# Revit family: Square Diffuser-Round Neck-Return
name_source: partatom
category: Air Terminals
revit_build: Autodesk Revit MEP 2013 (Build: 20120221_2030(x64)
units: mm (PartAtom-declared; Revit-internal decimal feet)

## types (5) — shared parameters

## per-type parameters (varying)
| type | Diffuser Neck Length | Diffuser Neck Width | Diffuser Total Length | Diffuser Total Width | Max Flow |
| 600x600-Square Diffuser-Round Neck-Return | 450 mm | 450 mm | 600 mm  [stored 1.9685 ft] | 600 mm  [stored 1.9685 ft] | 70.0 L/s |
| 525x525-Square Diffuser-Round Neck-Return | 375 mm | 375 mm | 525 mm | 525 mm | 70.0 L/s |
| 450x450-Square Diffuser-Round Neck-Return | 300 mm | 300 mm | 450 mm  [stored 1.47638 ft] | 450 mm  [stored 1.47638 ft] | 70.0 L/s |
| 300x300-Square Diffuser-Round Neck-Return | 225 mm | 225 mm | 375 mm  [stored 1.23031 ft] | 375 mm  [stored 1.23031 ft] | 30.0 L/s |
| 375x375-Square Diffuser-Round Neck-Return | 225 mm | 225 mm | 375 mm  [stored 1.23031 ft] | 375 mm  [stored 1.23031 ft] | 70.0 L/s |

note: [stored X ft] marks values corroborated as IEEE doubles in the binary element streams (Revit-internal decimal feet)

## geometry (parser evidence)
native form markers: Sweep x8
no freeform markers — native parametric forms only
